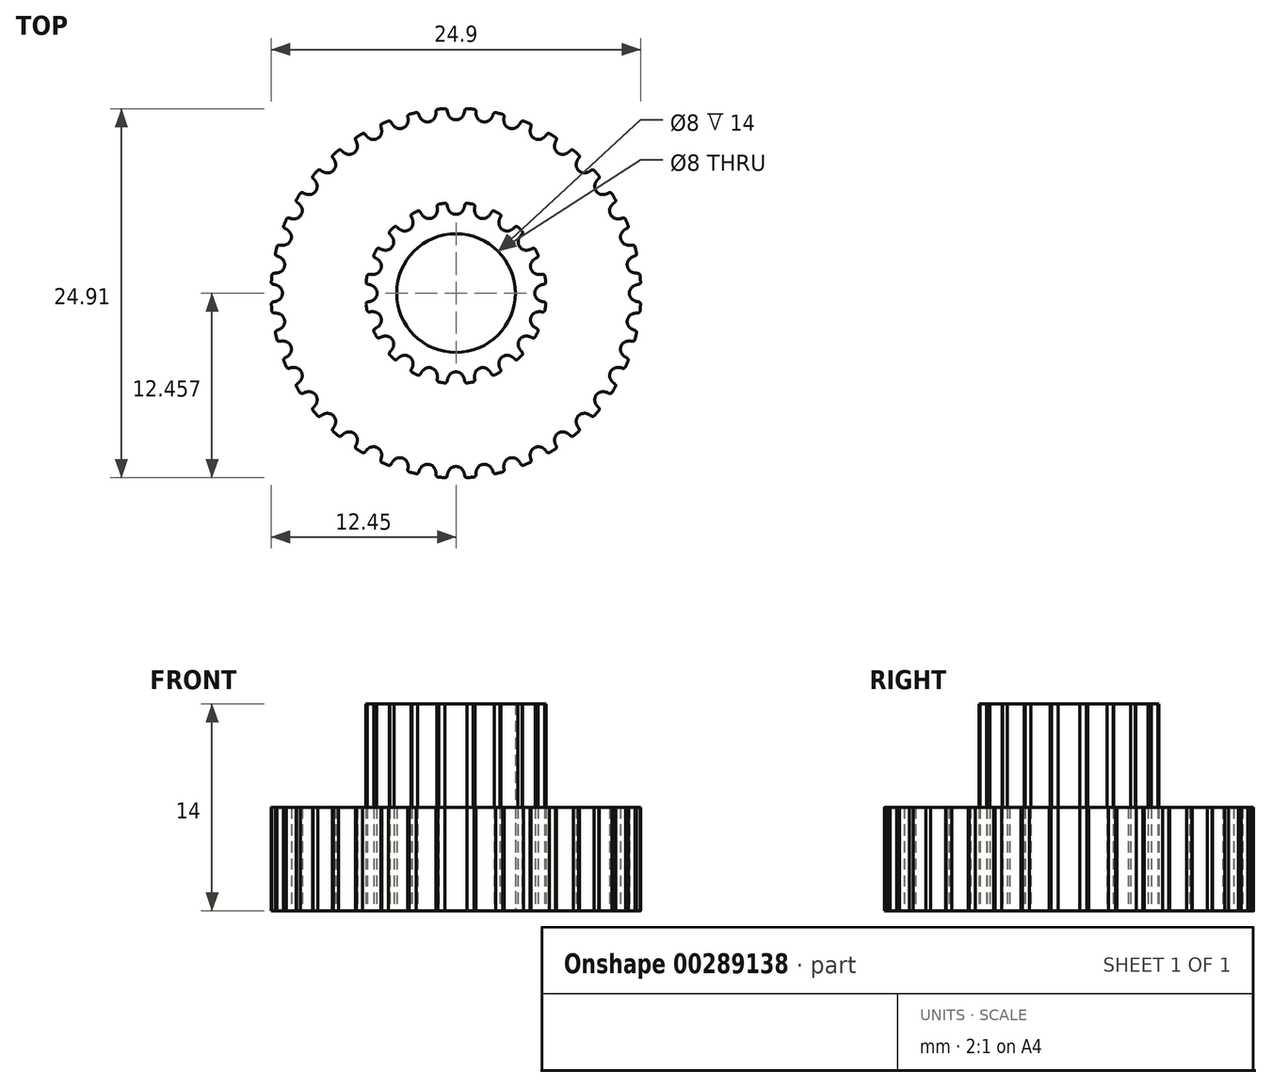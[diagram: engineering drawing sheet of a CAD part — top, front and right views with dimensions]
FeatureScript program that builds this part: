
annotation { "Feature Type Name" : "Feature", "Feature Type Description" : "" }
export const myFeature = defineFeature(function(context is Context, id is Id, definition is map)
    precondition{}
    {
        {
            var Q0;
            Q0=qCreatedBy(makeId("Top.planeOp"),FACE);
            var sketch = newSketch(context, id + "F0", { "sketchPlane" : qUnion([Q0])});
            skLineSegment(sketch, "E0", {"start": v(0, 0) * mm, "end": v(0, -1.46) * mm, "construction": true});
            skArc(sketch, "E1", {"start": v(1.22, 12.21) * mm, "mid": v(0.98, 12.23) * mm, "end": v(0.74, 12.25) * mm});
            skArc(sketch, "E2", {"start": v(-0.5, 11.81) * mm, "mid": v(-0.3, 11.58) * mm, "end": v(0, 11.5) * mm});
            skArc(sketch, "E3", {"start": v(-0.6, 12.12) * mm, "mid": v(-0.56, 11.96) * mm, "end": v(-0.5, 11.81) * mm});
            skArc(sketch, "E4", {"start": v(-0.6, 12.12) * mm, "mid": v(-0.64, 12.21) * mm, "end": v(-0.74, 12.25) * mm});
            skArc(sketch, "E5", {"start": v(0, 11.5) * mm, "mid": v(0.3, 11.58) * mm, "end": v(0.5, 11.81) * mm});
            skArc(sketch, "E6", {"start": v(0.5, 11.81) * mm, "mid": v(0.56, 11.96) * mm, "end": v(0.6, 12.12) * mm});
            skArc(sketch, "E7", {"start": v(0.74, 12.25) * mm, "mid": v(0.64, 12.21) * mm, "end": v(0.6, 12.12) * mm});
            skArc(sketch, "E8", {"start": v(-2.37, 11.59) * mm, "mid": v(-2.13, 11.4) * mm, "end": v(-1.83, 11.36) * mm});
            skArc(sketch, "E9", {"start": v(-2.51, 11.88) * mm, "mid": v(-2.45, 11.73) * mm, "end": v(-2.37, 11.59) * mm});
            skArc(sketch, "E10", {"start": v(-2.51, 11.88) * mm, "mid": v(-2.58, 11.96) * mm, "end": v(-2.68, 11.98) * mm});
            skArc(sketch, "E11", {"start": v(-1.83, 11.36) * mm, "mid": v(-1.55, 11.49) * mm, "end": v(-1.39, 11.74) * mm});
            skArc(sketch, "E12", {"start": v(-1.39, 11.74) * mm, "mid": v(-1.35, 11.9) * mm, "end": v(-1.34, 12.06) * mm});
            skArc(sketch, "E13", {"start": v(-1.22, 12.21) * mm, "mid": v(-1.3, 12.16) * mm, "end": v(-1.34, 12.06) * mm});
            skArc(sketch, "E14", {"start": v(-4.19, 11.07) * mm, "mid": v(-3.92, 10.92) * mm, "end": v(-3.62, 10.93) * mm});
            skArc(sketch, "E15", {"start": v(-4.37, 11.33) * mm, "mid": v(-4.29, 11.2) * mm, "end": v(-4.19, 11.07) * mm});
            skArc(sketch, "E16", {"start": v(-4.37, 11.33) * mm, "mid": v(-4.45, 11.4) * mm, "end": v(-4.55, 11.41) * mm});
            skArc(sketch, "E17", {"start": v(-3.62, 10.93) * mm, "mid": v(-3.36, 11.1) * mm, "end": v(-3.24, 11.38) * mm});
            skArc(sketch, "E18", {"start": v(-3.24, 11.38) * mm, "mid": v(-3.23, 11.54) * mm, "end": v(-3.25, 11.7) * mm});
            skArc(sketch, "E19", {"start": v(-3.14, 11.87) * mm, "mid": v(-3.23, 11.8) * mm, "end": v(-3.25, 11.7) * mm});
            skArc(sketch, "E20", {"start": v(-5.9, 10.28) * mm, "mid": v(-5.61, 10.17) * mm, "end": v(-5.31, 10.22) * mm});
            skArc(sketch, "E21", {"start": v(-6.12, 10.5) * mm, "mid": v(-6.02, 10.38) * mm, "end": v(-5.9, 10.28) * mm});
            skArc(sketch, "E22", {"start": v(-6.12, 10.5) * mm, "mid": v(-6.2, 10.57) * mm, "end": v(-6.31, 10.56) * mm});
            skArc(sketch, "E23", {"start": v(-5.31, 10.22) * mm, "mid": v(-5.09, 10.43) * mm, "end": v(-5.01, 10.73) * mm});
            skArc(sketch, "E24", {"start": v(-5.01, 10.73) * mm, "mid": v(-5.03, 10.89) * mm, "end": v(-5.07, 11.05) * mm});
            skArc(sketch, "E25", {"start": v(-5, 11.23) * mm, "mid": v(-5.07, 11.15) * mm, "end": v(-5.07, 11.05) * mm});
            skArc(sketch, "E26", {"start": v(-7.47, 9.22) * mm, "mid": v(-7.17, 9.16) * mm, "end": v(-6.88, 9.27) * mm});
            skArc(sketch, "E27", {"start": v(-7.72, 9.42) * mm, "mid": v(-7.6, 9.31) * mm, "end": v(-7.47, 9.22) * mm});
            skArc(sketch, "E28", {"start": v(-7.72, 9.42) * mm, "mid": v(-7.82, 9.46) * mm, "end": v(-7.92, 9.44) * mm});
            skArc(sketch, "E29", {"start": v(-6.88, 9.27) * mm, "mid": v(-6.7, 9.5) * mm, "end": v(-6.66, 9.81) * mm});
            skArc(sketch, "E30", {"start": v(-6.66, 9.81) * mm, "mid": v(-6.7, 9.97) * mm, "end": v(-6.76, 10.11) * mm});
            skArc(sketch, "E31", {"start": v(-6.72, 10.3) * mm, "mid": v(-6.78, 10.22) * mm, "end": v(-6.76, 10.11) * mm});
            skArc(sketch, "E32", {"start": v(-8.85, 7.94) * mm, "mid": v(-8.54, 7.92) * mm, "end": v(-8.28, 8.07) * mm});
            skArc(sketch, "E33", {"start": v(-9.13, 8.1) * mm, "mid": v(-9, 8) * mm, "end": v(-8.85, 7.94) * mm});
            skArc(sketch, "E34", {"start": v(-9.13, 8.1) * mm, "mid": v(-9.23, 8.12) * mm, "end": v(-9.33, 8.08) * mm});
            skArc(sketch, "E35", {"start": v(-8.28, 8.07) * mm, "mid": v(-8.13, 8.34) * mm, "end": v(-8.14, 8.65) * mm});
            skArc(sketch, "E36", {"start": v(-8.14, 8.65) * mm, "mid": v(-8.2, 8.8) * mm, "end": v(-8.3, 8.93) * mm});
            skArc(sketch, "E37", {"start": v(-8.28, 9.13) * mm, "mid": v(-8.33, 9.03) * mm, "end": v(-8.3, 8.93) * mm});
            skArc(sketch, "E38", {"start": v(-10.01, 6.46) * mm, "mid": v(-9.7, 6.49) * mm, "end": v(-9.47, 6.68) * mm});
            skArc(sketch, "E39", {"start": v(-10.32, 6.56) * mm, "mid": v(-10.17, 6.5) * mm, "end": v(-10.01, 6.46) * mm});
            skArc(sketch, "E40", {"start": v(-10.32, 6.56) * mm, "mid": v(-10.42, 6.58) * mm, "end": v(-10.5, 6.52) * mm});
            skArc(sketch, "E41", {"start": v(-9.47, 6.68) * mm, "mid": v(-9.36, 6.96) * mm, "end": v(-9.43, 7.26) * mm});
            skArc(sketch, "E42", {"start": v(-9.43, 7.26) * mm, "mid": v(-9.51, 7.4) * mm, "end": v(-9.62, 7.52) * mm});
            skArc(sketch, "E43", {"start": v(-9.64, 7.72) * mm, "mid": v(-9.67, 7.61) * mm, "end": v(-9.62, 7.52) * mm});
            skArc(sketch, "E44", {"start": v(-10.93, 4.8) * mm, "mid": v(-10.64, 4.89) * mm, "end": v(-10.43, 5.11) * mm});
            skArc(sketch, "E45", {"start": v(-11.25, 4.86) * mm, "mid": v(-11.1, 4.82) * mm, "end": v(-10.93, 4.8) * mm});
            skArc(sketch, "E46", {"start": v(-11.25, 4.86) * mm, "mid": v(-11.35, 4.86) * mm, "end": v(-11.43, 4.8) * mm});
            skArc(sketch, "E47", {"start": v(-10.43, 5.11) * mm, "mid": v(-10.37, 5.41) * mm, "end": v(-10.48, 5.7) * mm});
            skArc(sketch, "E48", {"start": v(-10.48, 5.7) * mm, "mid": v(-10.59, 5.82) * mm, "end": v(-10.71, 5.92) * mm});
            skArc(sketch, "E49", {"start": v(-10.76, 6.11) * mm, "mid": v(-10.77, 6) * mm, "end": v(-10.71, 5.92) * mm});
            skArc(sketch, "E50", {"start": v(-11.58, 3.04) * mm, "mid": v(-11.3, 3.16) * mm, "end": v(-11.13, 3.41) * mm});
            skArc(sketch, "E51", {"start": v(-11.9, 3.04) * mm, "mid": v(-11.74, 3.03) * mm, "end": v(-11.58, 3.04) * mm});
            skArc(sketch, "E52", {"start": v(-11.9, 3.04) * mm, "mid": v(-12, 3.02) * mm, "end": v(-12.07, 2.94) * mm});
            skArc(sketch, "E53", {"start": v(-11.13, 3.41) * mm, "mid": v(-11.12, 3.72) * mm, "end": v(-11.27, 3.98) * mm});
            skArc(sketch, "E54", {"start": v(-11.27, 3.98) * mm, "mid": v(-11.4, 4.09) * mm, "end": v(-11.54, 4.17) * mm});
            skArc(sketch, "E55", {"start": v(-11.61, 4.35) * mm, "mid": v(-11.6, 4.24) * mm, "end": v(-11.54, 4.17) * mm});
            skArc(sketch, "E56", {"start": v(-11.94, 1.18) * mm, "mid": v(-11.69, 1.35) * mm, "end": v(-11.56, 1.63) * mm});
            skArc(sketch, "E57", {"start": v(-12.26, 1.14) * mm, "mid": v(-12.1, 1.15) * mm, "end": v(-11.94, 1.18) * mm});
            skArc(sketch, "E58", {"start": v(-12.26, 1.14) * mm, "mid": v(-12.36, 1.1) * mm, "end": v(-12.42, 1.01) * mm});
            skArc(sketch, "E59", {"start": v(-11.56, 1.63) * mm, "mid": v(-11.6, 1.93) * mm, "end": v(-11.79, 2.17) * mm});
            skArc(sketch, "E60", {"start": v(-11.79, 2.17) * mm, "mid": v(-11.93, 2.25) * mm, "end": v(-12.08, 2.3) * mm});
            skArc(sketch, "E61", {"start": v(-12.18, 2.48) * mm, "mid": v(-12.16, 2.37) * mm, "end": v(-12.08, 2.3) * mm});
            skArc(sketch, "E62", {"start": v(-12.01, -0.7) * mm, "mid": v(-11.79, -0.5) * mm, "end": v(-11.7, -0.2) * mm});
            skArc(sketch, "E63", {"start": v(-12.32, -0.8) * mm, "mid": v(-12.16, -0.76) * mm, "end": v(-12.01, -0.7) * mm});
            skArc(sketch, "E64", {"start": v(-12.32, -0.8) * mm, "mid": v(-12.42, -0.84) * mm, "end": v(-12.45, -0.94) * mm});
            skArc(sketch, "E65", {"start": v(-11.7, -0.2) * mm, "mid": v(-11.79, 0.1) * mm, "end": v(-12.01, 0.3) * mm});
            skArc(sketch, "E66", {"start": v(-12.01, 0.3) * mm, "mid": v(-12.16, 0.35) * mm, "end": v(-12.32, 0.39) * mm});
            skArc(sketch, "E67", {"start": v(-12.45, 0.54) * mm, "mid": v(-12.42, 0.44) * mm, "end": v(-12.32, 0.39) * mm});
            skArc(sketch, "E68", {"start": v(-11.79, -2.58) * mm, "mid": v(-11.6, -2.34) * mm, "end": v(-11.56, -2.03) * mm});
            skArc(sketch, "E69", {"start": v(-12.08, -2.71) * mm, "mid": v(-11.93, -2.66) * mm, "end": v(-11.79, -2.58) * mm});
            skArc(sketch, "E70", {"start": v(-12.08, -2.71) * mm, "mid": v(-12.16, -2.78) * mm, "end": v(-12.18, -2.88) * mm});
            skArc(sketch, "E71", {"start": v(-11.56, -2.03) * mm, "mid": v(-11.69, -1.76) * mm, "end": v(-11.94, -1.59) * mm});
            skArc(sketch, "E72", {"start": v(-11.94, -1.59) * mm, "mid": v(-12.1, -1.56) * mm, "end": v(-12.26, -1.55) * mm});
            skArc(sketch, "E73", {"start": v(-12.42, -1.42) * mm, "mid": v(-12.36, -1.51) * mm, "end": v(-12.26, -1.55) * mm});
            skArc(sketch, "E74", {"start": v(-11.27, -4.4) * mm, "mid": v(-11.12, -4.13) * mm, "end": v(-11.13, -3.82) * mm});
            skArc(sketch, "E75", {"start": v(-11.54, -4.57) * mm, "mid": v(-11.4, -4.5) * mm, "end": v(-11.27, -4.4) * mm});
            skArc(sketch, "E76", {"start": v(-11.54, -4.57) * mm, "mid": v(-11.6, -4.65) * mm, "end": v(-11.61, -4.75) * mm});
            skArc(sketch, "E77", {"start": v(-11.13, -3.82) * mm, "mid": v(-11.3, -3.57) * mm, "end": v(-11.58, -3.44) * mm});
            skArc(sketch, "E78", {"start": v(-11.58, -3.44) * mm, "mid": v(-11.74, -3.43) * mm, "end": v(-11.9, -3.45) * mm});
            skArc(sketch, "E79", {"start": v(-12.07, -3.35) * mm, "mid": v(-12, -3.43) * mm, "end": v(-11.9, -3.45) * mm});
            skArc(sketch, "E80", {"start": v(-10.48, -6.1) * mm, "mid": v(-10.37, -5.82) * mm, "end": v(-10.43, -5.52) * mm});
            skArc(sketch, "E81", {"start": v(-10.71, -6.32) * mm, "mid": v(-10.59, -6.22) * mm, "end": v(-10.48, -6.1) * mm});
            skArc(sketch, "E82", {"start": v(-10.71, -6.32) * mm, "mid": v(-10.77, -6.41) * mm, "end": v(-10.76, -6.52) * mm});
            skArc(sketch, "E83", {"start": v(-10.43, -5.52) * mm, "mid": v(-10.64, -5.3) * mm, "end": v(-10.93, -5.21) * mm});
            skArc(sketch, "E84", {"start": v(-10.93, -5.21) * mm, "mid": v(-11.1, -5.23) * mm, "end": v(-11.25, -5.27) * mm});
            skArc(sketch, "E85", {"start": v(-11.43, -5.2) * mm, "mid": v(-11.35, -5.27) * mm, "end": v(-11.25, -5.27) * mm});
            skArc(sketch, "E86", {"start": v(-9.43, -7.67) * mm, "mid": v(-9.36, -7.37) * mm, "end": v(-9.47, -7.08) * mm});
            skArc(sketch, "E87", {"start": v(-9.62, -7.92) * mm, "mid": v(-9.51, -7.8) * mm, "end": v(-9.43, -7.67) * mm});
            skArc(sketch, "E88", {"start": v(-9.62, -7.92) * mm, "mid": v(-9.67, -8.02) * mm, "end": v(-9.64, -8.12) * mm});
            skArc(sketch, "E89", {"start": v(-9.47, -7.08) * mm, "mid": v(-9.7, -6.9) * mm, "end": v(-10.01, -6.86) * mm});
            skArc(sketch, "E90", {"start": v(-10.01, -6.86) * mm, "mid": v(-10.17, -6.9) * mm, "end": v(-10.32, -6.97) * mm});
            skArc(sketch, "E91", {"start": v(-10.5, -6.92) * mm, "mid": v(-10.42, -6.98) * mm, "end": v(-10.32, -6.97) * mm});
            skArc(sketch, "E92", {"start": v(-8.14, -9.05) * mm, "mid": v(-8.13, -8.75) * mm, "end": v(-8.28, -8.48) * mm});
            skArc(sketch, "E93", {"start": v(-8.3, -9.33) * mm, "mid": v(-8.2, -9.2) * mm, "end": v(-8.14, -9.05) * mm});
            skArc(sketch, "E94", {"start": v(-8.3, -9.33) * mm, "mid": v(-8.33, -9.44) * mm, "end": v(-8.28, -9.53) * mm});
            skArc(sketch, "E95", {"start": v(-8.28, -8.48) * mm, "mid": v(-8.54, -8.33) * mm, "end": v(-8.85, -8.35) * mm});
            skArc(sketch, "E96", {"start": v(-8.85, -8.35) * mm, "mid": v(-9, -8.41) * mm, "end": v(-9.13, -8.5) * mm});
            skArc(sketch, "E97", {"start": v(-9.33, -8.49) * mm, "mid": v(-9.23, -8.53) * mm, "end": v(-9.13, -8.5) * mm});
            skArc(sketch, "E98", {"start": v(-6.66, -10.22) * mm, "mid": v(-6.7, -9.91) * mm, "end": v(-6.88, -9.67) * mm});
            skArc(sketch, "E99", {"start": v(-6.76, -10.52) * mm, "mid": v(-6.7, -10.37) * mm, "end": v(-6.66, -10.22) * mm});
            skArc(sketch, "E100", {"start": v(-6.76, -10.52) * mm, "mid": v(-6.78, -10.62) * mm, "end": v(-6.72, -10.71) * mm});
            skArc(sketch, "E101", {"start": v(-6.88, -9.67) * mm, "mid": v(-7.17, -9.57) * mm, "end": v(-7.47, -9.63) * mm});
            skArc(sketch, "E102", {"start": v(-7.47, -9.63) * mm, "mid": v(-7.6, -9.72) * mm, "end": v(-7.72, -9.82) * mm});
            skArc(sketch, "E103", {"start": v(-7.92, -9.84) * mm, "mid": v(-7.82, -9.87) * mm, "end": v(-7.72, -9.82) * mm});
            skArc(sketch, "E104", {"start": v(-5.01, -11.13) * mm, "mid": v(-5.09, -10.84) * mm, "end": v(-5.31, -10.63) * mm});
            skArc(sketch, "E105", {"start": v(-5.07, -11.45) * mm, "mid": v(-5.03, -11.3) * mm, "end": v(-5.01, -11.13) * mm});
            skArc(sketch, "E106", {"start": v(-5.07, -11.45) * mm, "mid": v(-5.07, -11.56) * mm, "end": v(-5, -11.63) * mm});
            skArc(sketch, "E107", {"start": v(-5.31, -10.63) * mm, "mid": v(-5.61, -10.57) * mm, "end": v(-5.9, -10.68) * mm});
            skArc(sketch, "E108", {"start": v(-5.9, -10.68) * mm, "mid": v(-6.02, -10.79) * mm, "end": v(-6.12, -10.91) * mm});
            skArc(sketch, "E109", {"start": v(-6.31, -10.96) * mm, "mid": v(-6.2, -10.97) * mm, "end": v(-6.12, -10.91) * mm});
            skArc(sketch, "E110", {"start": v(-3.24, -11.78) * mm, "mid": v(-3.36, -11.5) * mm, "end": v(-3.62, -11.33) * mm});
            skArc(sketch, "E111", {"start": v(-3.25, -12.1) * mm, "mid": v(-3.23, -11.94) * mm, "end": v(-3.24, -11.78) * mm});
            skArc(sketch, "E112", {"start": v(-3.25, -12.1) * mm, "mid": v(-3.23, -12.2) * mm, "end": v(-3.14, -12.28) * mm});
            skArc(sketch, "E113", {"start": v(-3.62, -11.33) * mm, "mid": v(-3.92, -11.32) * mm, "end": v(-4.19, -11.48) * mm});
            skArc(sketch, "E114", {"start": v(-4.19, -11.48) * mm, "mid": v(-4.29, -11.6) * mm, "end": v(-4.37, -11.74) * mm});
            skArc(sketch, "E115", {"start": v(-4.55, -11.82) * mm, "mid": v(-4.45, -11.81) * mm, "end": v(-4.37, -11.74) * mm});
            skArc(sketch, "E116", {"start": v(-1.39, -12.15) * mm, "mid": v(-1.55, -11.9) * mm, "end": v(-1.83, -11.76) * mm});
            skArc(sketch, "E117", {"start": v(-1.34, -12.47) * mm, "mid": v(-1.35, -12.3) * mm, "end": v(-1.39, -12.15) * mm});
            skArc(sketch, "E118", {"start": v(-1.34, -12.47) * mm, "mid": v(-1.3, -12.57) * mm, "end": v(-1.22, -12.62) * mm});
            skArc(sketch, "E119", {"start": v(-1.83, -11.76) * mm, "mid": v(-2.13, -11.8) * mm, "end": v(-2.37, -12) * mm});
            skArc(sketch, "E120", {"start": v(-2.37, -12) * mm, "mid": v(-2.45, -12.13) * mm, "end": v(-2.51, -12.28) * mm});
            skArc(sketch, "E121", {"start": v(-2.68, -12.39) * mm, "mid": v(-2.58, -12.37) * mm, "end": v(-2.51, -12.28) * mm});
            skArc(sketch, "E122", {"start": v(0.5, -12.22) * mm, "mid": v(0.3, -12) * mm, "end": v(0, -11.9) * mm});
            skArc(sketch, "E123", {"start": v(0.6, -12.53) * mm, "mid": v(0.56, -12.37) * mm, "end": v(0.5, -12.22) * mm});
            skArc(sketch, "E124", {"start": v(0.6, -12.53) * mm, "mid": v(0.64, -12.62) * mm, "end": v(0.74, -12.66) * mm});
            skArc(sketch, "E125", {"start": v(0, -11.9) * mm, "mid": v(-0.3, -12) * mm, "end": v(-0.5, -12.22) * mm});
            skArc(sketch, "E126", {"start": v(-0.5, -12.22) * mm, "mid": v(-0.56, -12.37) * mm, "end": v(-0.6, -12.53) * mm});
            skArc(sketch, "E127", {"start": v(-0.74, -12.66) * mm, "mid": v(-0.64, -12.62) * mm, "end": v(-0.6, -12.53) * mm});
            skArc(sketch, "E128", {"start": v(2.37, -12) * mm, "mid": v(2.13, -11.8) * mm, "end": v(1.83, -11.76) * mm});
            skArc(sketch, "E129", {"start": v(2.51, -12.28) * mm, "mid": v(2.45, -12.13) * mm, "end": v(2.37, -12) * mm});
            skArc(sketch, "E130", {"start": v(2.51, -12.28) * mm, "mid": v(2.58, -12.37) * mm, "end": v(2.68, -12.39) * mm});
            skArc(sketch, "E131", {"start": v(1.83, -11.76) * mm, "mid": v(1.55, -11.9) * mm, "end": v(1.39, -12.15) * mm});
            skArc(sketch, "E132", {"start": v(1.39, -12.15) * mm, "mid": v(1.35, -12.3) * mm, "end": v(1.34, -12.47) * mm});
            skArc(sketch, "E133", {"start": v(1.22, -12.62) * mm, "mid": v(1.3, -12.57) * mm, "end": v(1.34, -12.47) * mm});
            skArc(sketch, "E134", {"start": v(4.19, -11.48) * mm, "mid": v(3.92, -11.32) * mm, "end": v(3.62, -11.33) * mm});
            skArc(sketch, "E135", {"start": v(4.37, -11.74) * mm, "mid": v(4.29, -11.6) * mm, "end": v(4.19, -11.48) * mm});
            skArc(sketch, "E136", {"start": v(4.37, -11.74) * mm, "mid": v(4.45, -11.81) * mm, "end": v(4.55, -11.82) * mm});
            skArc(sketch, "E137", {"start": v(3.62, -11.33) * mm, "mid": v(3.36, -11.5) * mm, "end": v(3.24, -11.78) * mm});
            skArc(sketch, "E138", {"start": v(3.24, -11.78) * mm, "mid": v(3.23, -11.94) * mm, "end": v(3.25, -12.1) * mm});
            skArc(sketch, "E139", {"start": v(3.14, -12.28) * mm, "mid": v(3.23, -12.2) * mm, "end": v(3.25, -12.1) * mm});
            skArc(sketch, "E140", {"start": v(5.9, -10.68) * mm, "mid": v(5.61, -10.57) * mm, "end": v(5.31, -10.63) * mm});
            skArc(sketch, "E141", {"start": v(6.12, -10.91) * mm, "mid": v(6.02, -10.79) * mm, "end": v(5.9, -10.68) * mm});
            skArc(sketch, "E142", {"start": v(6.12, -10.91) * mm, "mid": v(6.2, -10.97) * mm, "end": v(6.31, -10.96) * mm});
            skArc(sketch, "E143", {"start": v(5.31, -10.63) * mm, "mid": v(5.09, -10.84) * mm, "end": v(5.01, -11.13) * mm});
            skArc(sketch, "E144", {"start": v(5.01, -11.13) * mm, "mid": v(5.03, -11.3) * mm, "end": v(5.07, -11.45) * mm});
            skArc(sketch, "E145", {"start": v(5, -11.63) * mm, "mid": v(5.07, -11.56) * mm, "end": v(5.07, -11.45) * mm});
            skArc(sketch, "E146", {"start": v(7.47, -9.63) * mm, "mid": v(7.17, -9.57) * mm, "end": v(6.88, -9.67) * mm});
            skArc(sketch, "E147", {"start": v(7.72, -9.82) * mm, "mid": v(7.6, -9.72) * mm, "end": v(7.47, -9.63) * mm});
            skArc(sketch, "E148", {"start": v(7.72, -9.82) * mm, "mid": v(7.82, -9.87) * mm, "end": v(7.92, -9.84) * mm});
            skArc(sketch, "E149", {"start": v(6.88, -9.67) * mm, "mid": v(6.7, -9.91) * mm, "end": v(6.66, -10.22) * mm});
            skArc(sketch, "E150", {"start": v(6.66, -10.22) * mm, "mid": v(6.7, -10.37) * mm, "end": v(6.76, -10.52) * mm});
            skArc(sketch, "E151", {"start": v(6.72, -10.71) * mm, "mid": v(6.78, -10.62) * mm, "end": v(6.76, -10.52) * mm});
            skArc(sketch, "E152", {"start": v(8.85, -8.35) * mm, "mid": v(8.54, -8.33) * mm, "end": v(8.28, -8.48) * mm});
            skArc(sketch, "E153", {"start": v(9.13, -8.5) * mm, "mid": v(9, -8.41) * mm, "end": v(8.85, -8.35) * mm});
            skArc(sketch, "E154", {"start": v(9.13, -8.5) * mm, "mid": v(9.23, -8.53) * mm, "end": v(9.33, -8.49) * mm});
            skArc(sketch, "E155", {"start": v(8.28, -8.48) * mm, "mid": v(8.13, -8.75) * mm, "end": v(8.14, -9.05) * mm});
            skArc(sketch, "E156", {"start": v(8.14, -9.05) * mm, "mid": v(8.2, -9.2) * mm, "end": v(8.3, -9.33) * mm});
            skArc(sketch, "E157", {"start": v(8.28, -9.53) * mm, "mid": v(8.33, -9.44) * mm, "end": v(8.3, -9.33) * mm});
            skArc(sketch, "E158", {"start": v(10.01, -6.86) * mm, "mid": v(9.7, -6.9) * mm, "end": v(9.47, -7.08) * mm});
            skArc(sketch, "E159", {"start": v(10.32, -6.97) * mm, "mid": v(10.17, -6.9) * mm, "end": v(10.01, -6.86) * mm});
            skArc(sketch, "E160", {"start": v(10.32, -6.97) * mm, "mid": v(10.42, -6.98) * mm, "end": v(10.5, -6.92) * mm});
            skArc(sketch, "E161", {"start": v(9.47, -7.08) * mm, "mid": v(9.36, -7.37) * mm, "end": v(9.43, -7.67) * mm});
            skArc(sketch, "E162", {"start": v(9.43, -7.67) * mm, "mid": v(9.51, -7.8) * mm, "end": v(9.62, -7.92) * mm});
            skArc(sketch, "E163", {"start": v(9.64, -8.12) * mm, "mid": v(9.67, -8.02) * mm, "end": v(9.62, -7.92) * mm});
            skArc(sketch, "E164", {"start": v(10.93, -5.21) * mm, "mid": v(10.64, -5.3) * mm, "end": v(10.43, -5.52) * mm});
            skArc(sketch, "E165", {"start": v(11.25, -5.27) * mm, "mid": v(11.1, -5.23) * mm, "end": v(10.93, -5.21) * mm});
            skArc(sketch, "E166", {"start": v(11.25, -5.27) * mm, "mid": v(11.35, -5.27) * mm, "end": v(11.43, -5.2) * mm});
            skArc(sketch, "E167", {"start": v(10.43, -5.52) * mm, "mid": v(10.37, -5.82) * mm, "end": v(10.48, -6.1) * mm});
            skArc(sketch, "E168", {"start": v(10.48, -6.1) * mm, "mid": v(10.59, -6.22) * mm, "end": v(10.71, -6.32) * mm});
            skArc(sketch, "E169", {"start": v(10.76, -6.52) * mm, "mid": v(10.77, -6.41) * mm, "end": v(10.71, -6.32) * mm});
            skArc(sketch, "E170", {"start": v(11.58, -3.44) * mm, "mid": v(11.3, -3.57) * mm, "end": v(11.13, -3.82) * mm});
            skArc(sketch, "E171", {"start": v(11.9, -3.45) * mm, "mid": v(11.74, -3.43) * mm, "end": v(11.58, -3.44) * mm});
            skArc(sketch, "E172", {"start": v(11.9, -3.45) * mm, "mid": v(12, -3.43) * mm, "end": v(12.07, -3.35) * mm});
            skArc(sketch, "E173", {"start": v(11.13, -3.82) * mm, "mid": v(11.12, -4.13) * mm, "end": v(11.27, -4.4) * mm});
            skArc(sketch, "E174", {"start": v(11.27, -4.4) * mm, "mid": v(11.4, -4.5) * mm, "end": v(11.54, -4.57) * mm});
            skArc(sketch, "E175", {"start": v(11.61, -4.75) * mm, "mid": v(11.6, -4.65) * mm, "end": v(11.54, -4.57) * mm});
            skArc(sketch, "E176", {"start": v(11.94, -1.59) * mm, "mid": v(11.69, -1.76) * mm, "end": v(11.56, -2.03) * mm});
            skArc(sketch, "E177", {"start": v(12.26, -1.55) * mm, "mid": v(12.1, -1.56) * mm, "end": v(11.94, -1.59) * mm});
            skArc(sketch, "E178", {"start": v(12.26, -1.55) * mm, "mid": v(12.36, -1.51) * mm, "end": v(12.42, -1.42) * mm});
            skArc(sketch, "E179", {"start": v(11.56, -2.03) * mm, "mid": v(11.6, -2.34) * mm, "end": v(11.79, -2.58) * mm});
            skArc(sketch, "E180", {"start": v(11.79, -2.58) * mm, "mid": v(11.93, -2.66) * mm, "end": v(12.08, -2.71) * mm});
            skArc(sketch, "E181", {"start": v(12.18, -2.88) * mm, "mid": v(12.16, -2.78) * mm, "end": v(12.08, -2.71) * mm});
            skArc(sketch, "E182", {"start": v(12.01, 0.3) * mm, "mid": v(11.79, 0.1) * mm, "end": v(11.7, -0.2) * mm});
            skArc(sketch, "E183", {"start": v(12.32, 0.39) * mm, "mid": v(12.16, 0.35) * mm, "end": v(12.01, 0.3) * mm});
            skArc(sketch, "E184", {"start": v(12.32, 0.39) * mm, "mid": v(12.42, 0.44) * mm, "end": v(12.45, 0.54) * mm});
            skArc(sketch, "E185", {"start": v(11.7, -0.2) * mm, "mid": v(11.79, -0.5) * mm, "end": v(12.01, -0.7) * mm});
            skArc(sketch, "E186", {"start": v(12.01, -0.7) * mm, "mid": v(12.16, -0.76) * mm, "end": v(12.32, -0.8) * mm});
            skArc(sketch, "E187", {"start": v(12.45, -0.94) * mm, "mid": v(12.42, -0.84) * mm, "end": v(12.32, -0.8) * mm});
            skArc(sketch, "E188", {"start": v(11.79, 2.17) * mm, "mid": v(11.6, 1.93) * mm, "end": v(11.56, 1.63) * mm});
            skArc(sketch, "E189", {"start": v(12.08, 2.3) * mm, "mid": v(11.93, 2.25) * mm, "end": v(11.79, 2.17) * mm});
            skArc(sketch, "E190", {"start": v(12.08, 2.3) * mm, "mid": v(12.16, 2.37) * mm, "end": v(12.18, 2.48) * mm});
            skArc(sketch, "E191", {"start": v(11.56, 1.63) * mm, "mid": v(11.69, 1.35) * mm, "end": v(11.94, 1.18) * mm});
            skArc(sketch, "E192", {"start": v(11.94, 1.18) * mm, "mid": v(12.1, 1.15) * mm, "end": v(12.26, 1.14) * mm});
            skArc(sketch, "E193", {"start": v(12.42, 1.01) * mm, "mid": v(12.36, 1.1) * mm, "end": v(12.26, 1.14) * mm});
            skArc(sketch, "E194", {"start": v(11.27, 3.98) * mm, "mid": v(11.12, 3.72) * mm, "end": v(11.13, 3.41) * mm});
            skArc(sketch, "E195", {"start": v(11.54, 4.17) * mm, "mid": v(11.4, 4.09) * mm, "end": v(11.27, 3.98) * mm});
            skArc(sketch, "E196", {"start": v(11.54, 4.17) * mm, "mid": v(11.6, 4.24) * mm, "end": v(11.61, 4.35) * mm});
            skArc(sketch, "E197", {"start": v(11.13, 3.41) * mm, "mid": v(11.3, 3.16) * mm, "end": v(11.58, 3.04) * mm});
            skArc(sketch, "E198", {"start": v(11.58, 3.04) * mm, "mid": v(11.74, 3.03) * mm, "end": v(11.9, 3.04) * mm});
            skArc(sketch, "E199", {"start": v(12.07, 2.94) * mm, "mid": v(12, 3.02) * mm, "end": v(11.9, 3.04) * mm});
            skArc(sketch, "E200", {"start": v(10.48, 5.7) * mm, "mid": v(10.37, 5.41) * mm, "end": v(10.43, 5.11) * mm});
            skArc(sketch, "E201", {"start": v(10.71, 5.92) * mm, "mid": v(10.59, 5.82) * mm, "end": v(10.48, 5.7) * mm});
            skArc(sketch, "E202", {"start": v(10.71, 5.92) * mm, "mid": v(10.77, 6) * mm, "end": v(10.76, 6.11) * mm});
            skArc(sketch, "E203", {"start": v(10.43, 5.11) * mm, "mid": v(10.64, 4.89) * mm, "end": v(10.93, 4.8) * mm});
            skArc(sketch, "E204", {"start": v(10.93, 4.8) * mm, "mid": v(11.1, 4.82) * mm, "end": v(11.25, 4.86) * mm});
            skArc(sketch, "E205", {"start": v(11.43, 4.8) * mm, "mid": v(11.35, 4.86) * mm, "end": v(11.25, 4.86) * mm});
            skArc(sketch, "E206", {"start": v(9.43, 7.26) * mm, "mid": v(9.36, 6.96) * mm, "end": v(9.47, 6.68) * mm});
            skArc(sketch, "E207", {"start": v(9.62, 7.52) * mm, "mid": v(9.51, 7.4) * mm, "end": v(9.43, 7.26) * mm});
            skArc(sketch, "E208", {"start": v(9.62, 7.52) * mm, "mid": v(9.67, 7.61) * mm, "end": v(9.64, 7.72) * mm});
            skArc(sketch, "E209", {"start": v(9.47, 6.68) * mm, "mid": v(9.7, 6.49) * mm, "end": v(10.01, 6.46) * mm});
            skArc(sketch, "E210", {"start": v(10.01, 6.46) * mm, "mid": v(10.17, 6.5) * mm, "end": v(10.32, 6.56) * mm});
            skArc(sketch, "E211", {"start": v(10.5, 6.52) * mm, "mid": v(10.42, 6.58) * mm, "end": v(10.32, 6.56) * mm});
            skArc(sketch, "E212", {"start": v(8.14, 8.65) * mm, "mid": v(8.13, 8.34) * mm, "end": v(8.28, 8.07) * mm});
            skArc(sketch, "E213", {"start": v(8.3, 8.93) * mm, "mid": v(8.2, 8.8) * mm, "end": v(8.14, 8.65) * mm});
            skArc(sketch, "E214", {"start": v(8.3, 8.93) * mm, "mid": v(8.33, 9.03) * mm, "end": v(8.28, 9.13) * mm});
            skArc(sketch, "E215", {"start": v(8.28, 8.07) * mm, "mid": v(8.54, 7.92) * mm, "end": v(8.85, 7.94) * mm});
            skArc(sketch, "E216", {"start": v(8.85, 7.94) * mm, "mid": v(9, 8) * mm, "end": v(9.13, 8.1) * mm});
            skArc(sketch, "E217", {"start": v(9.33, 8.08) * mm, "mid": v(9.23, 8.12) * mm, "end": v(9.13, 8.1) * mm});
            skArc(sketch, "E218", {"start": v(6.66, 9.81) * mm, "mid": v(6.7, 9.5) * mm, "end": v(6.88, 9.27) * mm});
            skArc(sketch, "E219", {"start": v(6.76, 10.11) * mm, "mid": v(6.7, 9.97) * mm, "end": v(6.66, 9.81) * mm});
            skArc(sketch, "E220", {"start": v(6.76, 10.11) * mm, "mid": v(6.78, 10.22) * mm, "end": v(6.72, 10.3) * mm});
            skArc(sketch, "E221", {"start": v(6.88, 9.27) * mm, "mid": v(7.17, 9.16) * mm, "end": v(7.47, 9.22) * mm});
            skArc(sketch, "E222", {"start": v(7.47, 9.22) * mm, "mid": v(7.6, 9.31) * mm, "end": v(7.72, 9.42) * mm});
            skArc(sketch, "E223", {"start": v(7.92, 9.44) * mm, "mid": v(7.82, 9.46) * mm, "end": v(7.72, 9.42) * mm});
            skArc(sketch, "E224", {"start": v(5.01, 10.73) * mm, "mid": v(5.09, 10.43) * mm, "end": v(5.31, 10.22) * mm});
            skArc(sketch, "E225", {"start": v(5.07, 11.05) * mm, "mid": v(5.03, 10.89) * mm, "end": v(5.01, 10.73) * mm});
            skArc(sketch, "E226", {"start": v(5.07, 11.05) * mm, "mid": v(5.07, 11.15) * mm, "end": v(5, 11.23) * mm});
            skArc(sketch, "E227", {"start": v(5.31, 10.22) * mm, "mid": v(5.61, 10.17) * mm, "end": v(5.9, 10.28) * mm});
            skArc(sketch, "E228", {"start": v(5.9, 10.28) * mm, "mid": v(6.02, 10.38) * mm, "end": v(6.12, 10.5) * mm});
            skArc(sketch, "E229", {"start": v(6.31, 10.56) * mm, "mid": v(6.2, 10.57) * mm, "end": v(6.12, 10.5) * mm});
            skArc(sketch, "E230", {"start": v(3.24, 11.38) * mm, "mid": v(3.36, 11.1) * mm, "end": v(3.62, 10.93) * mm});
            skArc(sketch, "E231", {"start": v(3.25, 11.7) * mm, "mid": v(3.23, 11.54) * mm, "end": v(3.24, 11.38) * mm});
            skArc(sketch, "E232", {"start": v(3.25, 11.7) * mm, "mid": v(3.23, 11.8) * mm, "end": v(3.14, 11.87) * mm});
            skArc(sketch, "E233", {"start": v(3.62, 10.93) * mm, "mid": v(3.92, 10.92) * mm, "end": v(4.19, 11.07) * mm});
            skArc(sketch, "E234", {"start": v(4.19, 11.07) * mm, "mid": v(4.29, 11.2) * mm, "end": v(4.37, 11.33) * mm});
            skArc(sketch, "E235", {"start": v(4.55, 11.41) * mm, "mid": v(4.45, 11.4) * mm, "end": v(4.37, 11.33) * mm});
            skArc(sketch, "E236", {"start": v(1.39, 11.74) * mm, "mid": v(1.55, 11.49) * mm, "end": v(1.83, 11.36) * mm});
            skArc(sketch, "E237", {"start": v(1.34, 12.06) * mm, "mid": v(1.35, 11.9) * mm, "end": v(1.39, 11.74) * mm});
            skArc(sketch, "E238", {"start": v(1.34, 12.06) * mm, "mid": v(1.3, 12.16) * mm, "end": v(1.22, 12.21) * mm});
            skArc(sketch, "E239", {"start": v(1.83, 11.36) * mm, "mid": v(2.13, 11.4) * mm, "end": v(2.37, 11.59) * mm});
            skArc(sketch, "E240", {"start": v(2.37, 11.59) * mm, "mid": v(2.45, 11.73) * mm, "end": v(2.51, 11.88) * mm});
            skArc(sketch, "E241", {"start": v(2.68, 11.98) * mm, "mid": v(2.58, 11.96) * mm, "end": v(2.51, 11.88) * mm});
            skArc(sketch, "E242", {"start": v(-10.76, -6.52) * mm, "mid": v(-10.64, -6.72) * mm, "end": v(-10.5, -6.92) * mm});
            skArc(sketch, "E243", {"start": v(-9.64, -8.12) * mm, "mid": v(-9.49, -8.3) * mm, "end": v(-9.33, -8.49) * mm});
            skArc(sketch, "E244", {"start": v(-8.28, -9.53) * mm, "mid": v(-8.1, -9.69) * mm, "end": v(-7.92, -9.84) * mm});
            skArc(sketch, "E245", {"start": v(-6.72, -10.71) * mm, "mid": v(-6.52, -10.84) * mm, "end": v(-6.31, -10.96) * mm});
            skArc(sketch, "E246", {"start": v(-5, -11.63) * mm, "mid": v(-4.77, -11.73) * mm, "end": v(-4.55, -11.82) * mm});
            skArc(sketch, "E247", {"start": v(-3.14, -12.28) * mm, "mid": v(-2.91, -12.33) * mm, "end": v(-2.68, -12.39) * mm});
            skArc(sketch, "E248", {"start": v(-1.22, -12.62) * mm, "mid": v(-0.98, -12.64) * mm, "end": v(-0.74, -12.66) * mm});
            skArc(sketch, "E249", {"start": v(0.74, -12.66) * mm, "mid": v(0.98, -12.64) * mm, "end": v(1.22, -12.62) * mm});
            skArc(sketch, "E250", {"start": v(2.68, -12.39) * mm, "mid": v(2.91, -12.33) * mm, "end": v(3.14, -12.28) * mm});
            skArc(sketch, "E251", {"start": v(4.55, -11.82) * mm, "mid": v(4.77, -11.73) * mm, "end": v(5, -11.63) * mm});
            skArc(sketch, "E252", {"start": v(6.31, -10.96) * mm, "mid": v(6.52, -10.84) * mm, "end": v(6.72, -10.71) * mm});
            skArc(sketch, "E253", {"start": v(7.92, -9.84) * mm, "mid": v(8.1, -9.69) * mm, "end": v(8.28, -9.53) * mm});
            skArc(sketch, "E254", {"start": v(9.33, -8.49) * mm, "mid": v(9.49, -8.3) * mm, "end": v(9.64, -8.12) * mm});
            skArc(sketch, "E255", {"start": v(10.5, -6.92) * mm, "mid": v(10.64, -6.72) * mm, "end": v(10.76, -6.52) * mm});
            skArc(sketch, "E256", {"start": v(11.43, -5.2) * mm, "mid": v(11.53, -4.98) * mm, "end": v(11.61, -4.75) * mm});
            skArc(sketch, "E257", {"start": v(12.07, -3.35) * mm, "mid": v(12.13, -3.12) * mm, "end": v(12.18, -2.88) * mm});
            skArc(sketch, "E258", {"start": v(12.42, -1.42) * mm, "mid": v(12.44, -1.18) * mm, "end": v(12.45, -0.94) * mm});
            skArc(sketch, "E259", {"start": v(12.45, 0.54) * mm, "mid": v(12.44, 0.78) * mm, "end": v(12.42, 1.01) * mm});
            skArc(sketch, "E260", {"start": v(12.18, 2.48) * mm, "mid": v(12.13, 2.7) * mm, "end": v(12.07, 2.94) * mm});
            skArc(sketch, "E261", {"start": v(11.61, 4.35) * mm, "mid": v(11.53, 4.57) * mm, "end": v(11.43, 4.8) * mm});
            skArc(sketch, "E262", {"start": v(10.76, 6.11) * mm, "mid": v(10.64, 6.32) * mm, "end": v(10.5, 6.52) * mm});
            skArc(sketch, "E263", {"start": v(9.64, 7.72) * mm, "mid": v(9.49, 7.9) * mm, "end": v(9.33, 8.08) * mm});
            skArc(sketch, "E264", {"start": v(8.28, 9.13) * mm, "mid": v(8.1, 9.28) * mm, "end": v(7.92, 9.44) * mm});
            skArc(sketch, "E265", {"start": v(6.72, 10.3) * mm, "mid": v(6.52, 10.43) * mm, "end": v(6.31, 10.56) * mm});
            skArc(sketch, "E266", {"start": v(5, 11.23) * mm, "mid": v(4.77, 11.32) * mm, "end": v(4.55, 11.41) * mm});
            skArc(sketch, "E267", {"start": v(3.14, 11.87) * mm, "mid": v(2.91, 11.93) * mm, "end": v(2.68, 11.98) * mm});
            skArc(sketch, "E268", {"start": v(-0.74, 12.25) * mm, "mid": v(-0.98, 12.23) * mm, "end": v(-1.22, 12.21) * mm});
            skArc(sketch, "E269", {"start": v(-2.68, 11.98) * mm, "mid": v(-2.91, 11.93) * mm, "end": v(-3.14, 11.87) * mm});
            skArc(sketch, "E270", {"start": v(-4.55, 11.41) * mm, "mid": v(-4.77, 11.32) * mm, "end": v(-5, 11.23) * mm});
            skArc(sketch, "E271", {"start": v(-6.31, 10.56) * mm, "mid": v(-6.52, 10.43) * mm, "end": v(-6.72, 10.3) * mm});
            skArc(sketch, "E272", {"start": v(-7.92, 9.44) * mm, "mid": v(-8.1, 9.28) * mm, "end": v(-8.28, 9.13) * mm});
            skArc(sketch, "E273", {"start": v(-9.33, 8.08) * mm, "mid": v(-9.49, 7.9) * mm, "end": v(-9.64, 7.72) * mm});
            skArc(sketch, "E274", {"start": v(-10.5, 6.52) * mm, "mid": v(-10.64, 6.32) * mm, "end": v(-10.76, 6.11) * mm});
            skArc(sketch, "E275", {"start": v(-11.43, 4.8) * mm, "mid": v(-11.53, 4.57) * mm, "end": v(-11.61, 4.35) * mm});
            skArc(sketch, "E276", {"start": v(-12.07, 2.94) * mm, "mid": v(-12.13, 2.7) * mm, "end": v(-12.18, 2.48) * mm});
            skArc(sketch, "E277", {"start": v(-12.42, 1.01) * mm, "mid": v(-12.44, 0.78) * mm, "end": v(-12.45, 0.54) * mm});
            skArc(sketch, "E278", {"start": v(-12.45, -0.94) * mm, "mid": v(-12.44, -1.18) * mm, "end": v(-12.42, -1.42) * mm});
            skArc(sketch, "E279", {"start": v(-12.18, -2.88) * mm, "mid": v(-12.13, -3.12) * mm, "end": v(-12.07, -3.35) * mm});
            skArc(sketch, "E280", {"start": v(-11.61, -4.75) * mm, "mid": v(-11.53, -4.98) * mm, "end": v(-11.43, -5.2) * mm});
            skArc(sketch, "E281", {"start": v(-0.5, 5.42) * mm, "mid": v(-0.3, 5.2) * mm, "end": v(0, 5.11) * mm});
            skArc(sketch, "E282", {"start": v(-0.6, 5.73) * mm, "mid": v(-0.56, 5.57) * mm, "end": v(-0.5, 5.42) * mm});
            skArc(sketch, "E283", {"start": v(-0.6, 5.73) * mm, "mid": v(-0.64, 5.82) * mm, "end": v(-0.74, 5.86) * mm});
            skArc(sketch, "E284", {"start": v(0, 5.11) * mm, "mid": v(0.3, 5.2) * mm, "end": v(0.5, 5.42) * mm});
            skArc(sketch, "E285", {"start": v(0.5, 5.42) * mm, "mid": v(0.56, 5.57) * mm, "end": v(0.6, 5.73) * mm});
            skArc(sketch, "E286", {"start": v(0.74, 5.86) * mm, "mid": v(0.64, 5.82) * mm, "end": v(0.6, 5.73) * mm});
            skArc(sketch, "E287", {"start": v(-2.21, 5) * mm, "mid": v(-1.95, 4.84) * mm, "end": v(-1.64, 4.85) * mm});
            skArc(sketch, "E288", {"start": v(-2.4, 5.26) * mm, "mid": v(-2.32, 5.12) * mm, "end": v(-2.21, 5) * mm});
            skArc(sketch, "E289", {"start": v(-2.4, 5.26) * mm, "mid": v(-2.47, 5.33) * mm, "end": v(-2.58, 5.34) * mm});
            skArc(sketch, "E290", {"start": v(-1.64, 4.85) * mm, "mid": v(-1.39, 5.02) * mm, "end": v(-1.26, 5.3) * mm});
            skArc(sketch, "E291", {"start": v(-1.26, 5.3) * mm, "mid": v(-1.25, 5.46) * mm, "end": v(-1.27, 5.62) * mm});
            skArc(sketch, "E292", {"start": v(-1.17, 5.8) * mm, "mid": v(-1.25, 5.73) * mm, "end": v(-1.27, 5.62) * mm});
            skArc(sketch, "E293", {"start": v(-3.71, 4.06) * mm, "mid": v(-3.41, 4) * mm, "end": v(-3.12, 4.1) * mm});
            skArc(sketch, "E294", {"start": v(-3.97, 4.25) * mm, "mid": v(-3.85, 4.14) * mm, "end": v(-3.71, 4.06) * mm});
            skArc(sketch, "E295", {"start": v(-3.97, 4.25) * mm, "mid": v(-4.06, 4.3) * mm, "end": v(-4.16, 4.27) * mm});
            skArc(sketch, "E296", {"start": v(-3.12, 4.1) * mm, "mid": v(-2.94, 4.34) * mm, "end": v(-2.9, 4.64) * mm});
            skArc(sketch, "E297", {"start": v(-2.9, 4.64) * mm, "mid": v(-2.94, 4.8) * mm, "end": v(-3, 4.95) * mm});
            skArc(sketch, "E298", {"start": v(-2.97, 5.14) * mm, "mid": v(-3.02, 5.05) * mm, "end": v(-3, 4.95) * mm});
            skArc(sketch, "E299", {"start": v(-4.85, 2.7) * mm, "mid": v(-4.54, 2.73) * mm, "end": v(-4.3, 2.92) * mm});
            skArc(sketch, "E300", {"start": v(-5.15, 2.8) * mm, "mid": v(-5, 2.74) * mm, "end": v(-4.85, 2.7) * mm});
            skArc(sketch, "E301", {"start": v(-5.15, 2.8) * mm, "mid": v(-5.25, 2.82) * mm, "end": v(-5.34, 2.76) * mm});
            skArc(sketch, "E302", {"start": v(-4.3, 2.92) * mm, "mid": v(-4.2, 3.2) * mm, "end": v(-4.26, 3.5) * mm});
            skArc(sketch, "E303", {"start": v(-4.26, 3.5) * mm, "mid": v(-4.35, 3.64) * mm, "end": v(-4.45, 3.76) * mm});
            skArc(sketch, "E304", {"start": v(-4.47, 3.96) * mm, "mid": v(-4.5, 3.86) * mm, "end": v(-4.45, 3.76) * mm});
            skArc(sketch, "E305", {"start": v(-5.5, 1.06) * mm, "mid": v(-5.23, 1.19) * mm, "end": v(-5.05, 1.44) * mm});
            skArc(sketch, "E306", {"start": v(-5.83, 1.07) * mm, "mid": v(-5.67, 1.05) * mm, "end": v(-5.5, 1.06) * mm});
            skArc(sketch, "E307", {"start": v(-5.83, 1.07) * mm, "mid": v(-5.93, 1.05) * mm, "end": v(-6, 0.97) * mm});
            skArc(sketch, "E308", {"start": v(-5.05, 1.44) * mm, "mid": v(-5.04, 1.75) * mm, "end": v(-5.2, 2.01) * mm});
            skArc(sketch, "E309", {"start": v(-5.2, 2.01) * mm, "mid": v(-5.32, 2.11) * mm, "end": v(-5.46, 2.2) * mm});
            skArc(sketch, "E310", {"start": v(-5.54, 2.38) * mm, "mid": v(-5.53, 2.27) * mm, "end": v(-5.46, 2.2) * mm});
            skArc(sketch, "E311", {"start": v(-5.63, -0.7) * mm, "mid": v(-5.4, -0.5) * mm, "end": v(-5.31, -0.2) * mm});
            skArc(sketch, "E312", {"start": v(-5.93, -0.8) * mm, "mid": v(-5.78, -0.76) * mm, "end": v(-5.63, -0.7) * mm});
            skArc(sketch, "E313", {"start": v(-5.93, -0.8) * mm, "mid": v(-6.03, -0.84) * mm, "end": v(-6.06, -0.94) * mm});
            skArc(sketch, "E314", {"start": v(-5.31, -0.2) * mm, "mid": v(-5.4, 0.1) * mm, "end": v(-5.63, 0.3) * mm});
            skArc(sketch, "E315", {"start": v(-5.63, 0.3) * mm, "mid": v(-5.78, 0.35) * mm, "end": v(-5.93, 0.39) * mm});
            skArc(sketch, "E316", {"start": v(-6.06, 0.54) * mm, "mid": v(-6.03, 0.44) * mm, "end": v(-5.93, 0.39) * mm});
            skArc(sketch, "E317", {"start": v(-5.2, -2.42) * mm, "mid": v(-5.04, -2.15) * mm, "end": v(-5.05, -1.85) * mm});
            skArc(sketch, "E318", {"start": v(-5.46, -2.6) * mm, "mid": v(-5.32, -2.52) * mm, "end": v(-5.2, -2.42) * mm});
            skArc(sketch, "E319", {"start": v(-5.46, -2.6) * mm, "mid": v(-5.53, -2.68) * mm, "end": v(-5.54, -2.78) * mm});
            skArc(sketch, "E320", {"start": v(-5.05, -1.85) * mm, "mid": v(-5.23, -1.6) * mm, "end": v(-5.5, -1.47) * mm});
            skArc(sketch, "E321", {"start": v(-5.5, -1.47) * mm, "mid": v(-5.67, -1.46) * mm, "end": v(-5.83, -1.47) * mm});
            skArc(sketch, "E322", {"start": v(-6, -1.37) * mm, "mid": v(-5.93, -1.46) * mm, "end": v(-5.83, -1.47) * mm});
            skArc(sketch, "E323", {"start": v(-4.26, -3.91) * mm, "mid": v(-4.2, -3.61) * mm, "end": v(-4.3, -3.33) * mm});
            skArc(sketch, "E324", {"start": v(-4.45, -4.17) * mm, "mid": v(-4.35, -4.05) * mm, "end": v(-4.26, -3.91) * mm});
            skArc(sketch, "E325", {"start": v(-4.45, -4.17) * mm, "mid": v(-4.5, -4.26) * mm, "end": v(-4.47, -4.37) * mm});
            skArc(sketch, "E326", {"start": v(-4.3, -3.33) * mm, "mid": v(-4.54, -3.14) * mm, "end": v(-4.85, -3.1) * mm});
            skArc(sketch, "E327", {"start": v(-4.85, -3.1) * mm, "mid": v(-5, -3.15) * mm, "end": v(-5.15, -3.21) * mm});
            skArc(sketch, "E328", {"start": v(-5.34, -3.17) * mm, "mid": v(-5.25, -3.23) * mm, "end": v(-5.15, -3.21) * mm});
            skArc(sketch, "E329", {"start": v(-2.9, -5.05) * mm, "mid": v(-2.94, -4.74) * mm, "end": v(-3.12, -4.5) * mm});
            skArc(sketch, "E330", {"start": v(-3, -5.35) * mm, "mid": v(-2.94, -5.2) * mm, "end": v(-2.9, -5.05) * mm});
            skArc(sketch, "E331", {"start": v(-3, -5.35) * mm, "mid": v(-3.02, -5.46) * mm, "end": v(-2.97, -5.54) * mm});
            skArc(sketch, "E332", {"start": v(-3.12, -4.5) * mm, "mid": v(-3.41, -4.4) * mm, "end": v(-3.71, -4.46) * mm});
            skArc(sketch, "E333", {"start": v(-3.71, -4.46) * mm, "mid": v(-3.85, -4.55) * mm, "end": v(-3.97, -4.66) * mm});
            skArc(sketch, "E334", {"start": v(-4.16, -4.67) * mm, "mid": v(-4.06, -4.7) * mm, "end": v(-3.97, -4.66) * mm});
            skArc(sketch, "E335", {"start": v(-1.26, -5.7) * mm, "mid": v(-1.39, -5.43) * mm, "end": v(-1.64, -5.26) * mm});
            skArc(sketch, "E336", {"start": v(-1.27, -6.03) * mm, "mid": v(-1.25, -5.87) * mm, "end": v(-1.26, -5.7) * mm});
            skArc(sketch, "E337", {"start": v(-1.27, -6.03) * mm, "mid": v(-1.25, -6.13) * mm, "end": v(-1.17, -6.2) * mm});
            skArc(sketch, "E338", {"start": v(-1.64, -5.26) * mm, "mid": v(-1.95, -5.25) * mm, "end": v(-2.21, -5.4) * mm});
            skArc(sketch, "E339", {"start": v(-2.21, -5.4) * mm, "mid": v(-2.32, -5.52) * mm, "end": v(-2.4, -5.66) * mm});
            skArc(sketch, "E340", {"start": v(-2.58, -5.74) * mm, "mid": v(-2.47, -5.74) * mm, "end": v(-2.4, -5.66) * mm});
            skArc(sketch, "E341", {"start": v(0.5, -5.83) * mm, "mid": v(0.3, -5.6) * mm, "end": v(0, -5.52) * mm});
            skArc(sketch, "E342", {"start": v(0.6, -6.14) * mm, "mid": v(0.56, -5.98) * mm, "end": v(0.5, -5.83) * mm});
            skArc(sketch, "E343", {"start": v(0.6, -6.14) * mm, "mid": v(0.64, -6.23) * mm, "end": v(0.74, -6.27) * mm});
            skArc(sketch, "E344", {"start": v(0, -5.52) * mm, "mid": v(-0.3, -5.6) * mm, "end": v(-0.5, -5.83) * mm});
            skArc(sketch, "E345", {"start": v(-0.5, -5.83) * mm, "mid": v(-0.56, -5.98) * mm, "end": v(-0.6, -6.14) * mm});
            skArc(sketch, "E346", {"start": v(-0.74, -6.27) * mm, "mid": v(-0.64, -6.23) * mm, "end": v(-0.6, -6.14) * mm});
            skArc(sketch, "E347", {"start": v(2.21, -5.4) * mm, "mid": v(1.95, -5.25) * mm, "end": v(1.64, -5.26) * mm});
            skArc(sketch, "E348", {"start": v(2.4, -5.66) * mm, "mid": v(2.32, -5.52) * mm, "end": v(2.21, -5.4) * mm});
            skArc(sketch, "E349", {"start": v(2.4, -5.66) * mm, "mid": v(2.47, -5.74) * mm, "end": v(2.58, -5.74) * mm});
            skArc(sketch, "E350", {"start": v(1.64, -5.26) * mm, "mid": v(1.39, -5.43) * mm, "end": v(1.26, -5.7) * mm});
            skArc(sketch, "E351", {"start": v(1.26, -5.7) * mm, "mid": v(1.25, -5.87) * mm, "end": v(1.27, -6.03) * mm});
            skArc(sketch, "E352", {"start": v(1.17, -6.2) * mm, "mid": v(1.25, -6.13) * mm, "end": v(1.27, -6.03) * mm});
            skArc(sketch, "E353", {"start": v(3.71, -4.46) * mm, "mid": v(3.41, -4.4) * mm, "end": v(3.12, -4.5) * mm});
            skArc(sketch, "E354", {"start": v(3.97, -4.66) * mm, "mid": v(3.85, -4.55) * mm, "end": v(3.71, -4.46) * mm});
            skArc(sketch, "E355", {"start": v(3.97, -4.66) * mm, "mid": v(4.06, -4.7) * mm, "end": v(4.16, -4.67) * mm});
            skArc(sketch, "E356", {"start": v(3.12, -4.5) * mm, "mid": v(2.94, -4.74) * mm, "end": v(2.9, -5.05) * mm});
            skArc(sketch, "E357", {"start": v(2.9, -5.05) * mm, "mid": v(2.94, -5.2) * mm, "end": v(3, -5.35) * mm});
            skArc(sketch, "E358", {"start": v(2.97, -5.54) * mm, "mid": v(3.02, -5.46) * mm, "end": v(3, -5.35) * mm});
            skArc(sketch, "E359", {"start": v(4.85, -3.1) * mm, "mid": v(4.54, -3.14) * mm, "end": v(4.3, -3.33) * mm});
            skArc(sketch, "E360", {"start": v(5.15, -3.21) * mm, "mid": v(5, -3.15) * mm, "end": v(4.85, -3.1) * mm});
            skArc(sketch, "E361", {"start": v(5.15, -3.21) * mm, "mid": v(5.25, -3.23) * mm, "end": v(5.34, -3.17) * mm});
            skArc(sketch, "E362", {"start": v(4.3, -3.33) * mm, "mid": v(4.2, -3.61) * mm, "end": v(4.26, -3.91) * mm});
            skArc(sketch, "E363", {"start": v(4.26, -3.91) * mm, "mid": v(4.35, -4.05) * mm, "end": v(4.45, -4.17) * mm});
            skArc(sketch, "E364", {"start": v(4.47, -4.37) * mm, "mid": v(4.5, -4.26) * mm, "end": v(4.45, -4.17) * mm});
            skArc(sketch, "E365", {"start": v(5.5, -1.47) * mm, "mid": v(5.23, -1.6) * mm, "end": v(5.05, -1.85) * mm});
            skArc(sketch, "E366", {"start": v(5.83, -1.47) * mm, "mid": v(5.67, -1.46) * mm, "end": v(5.5, -1.47) * mm});
            skArc(sketch, "E367", {"start": v(5.83, -1.47) * mm, "mid": v(5.93, -1.46) * mm, "end": v(6, -1.37) * mm});
            skArc(sketch, "E368", {"start": v(5.05, -1.85) * mm, "mid": v(5.04, -2.15) * mm, "end": v(5.2, -2.42) * mm});
            skArc(sketch, "E369", {"start": v(5.2, -2.42) * mm, "mid": v(5.32, -2.52) * mm, "end": v(5.46, -2.6) * mm});
            skArc(sketch, "E370", {"start": v(5.54, -2.78) * mm, "mid": v(5.53, -2.68) * mm, "end": v(5.46, -2.6) * mm});
            skArc(sketch, "E371", {"start": v(5.63, 0.3) * mm, "mid": v(5.4, 0.1) * mm, "end": v(5.31, -0.2) * mm});
            skArc(sketch, "E372", {"start": v(5.93, 0.39) * mm, "mid": v(5.78, 0.35) * mm, "end": v(5.63, 0.3) * mm});
            skArc(sketch, "E373", {"start": v(5.93, 0.39) * mm, "mid": v(6.03, 0.44) * mm, "end": v(6.06, 0.54) * mm});
            skArc(sketch, "E374", {"start": v(5.31, -0.2) * mm, "mid": v(5.4, -0.5) * mm, "end": v(5.63, -0.7) * mm});
            skArc(sketch, "E375", {"start": v(5.63, -0.7) * mm, "mid": v(5.78, -0.76) * mm, "end": v(5.93, -0.8) * mm});
            skArc(sketch, "E376", {"start": v(6.06, -0.94) * mm, "mid": v(6.03, -0.84) * mm, "end": v(5.93, -0.8) * mm});
            skArc(sketch, "E377", {"start": v(5.2, 2.01) * mm, "mid": v(5.04, 1.75) * mm, "end": v(5.05, 1.44) * mm});
            skArc(sketch, "E378", {"start": v(5.46, 2.2) * mm, "mid": v(5.32, 2.11) * mm, "end": v(5.2, 2.01) * mm});
            skArc(sketch, "E379", {"start": v(5.46, 2.2) * mm, "mid": v(5.53, 2.27) * mm, "end": v(5.54, 2.38) * mm});
            skArc(sketch, "E380", {"start": v(5.05, 1.44) * mm, "mid": v(5.23, 1.19) * mm, "end": v(5.5, 1.06) * mm});
            skArc(sketch, "E381", {"start": v(5.5, 1.06) * mm, "mid": v(5.67, 1.05) * mm, "end": v(5.83, 1.07) * mm});
            skArc(sketch, "E382", {"start": v(6, 0.97) * mm, "mid": v(5.93, 1.05) * mm, "end": v(5.83, 1.07) * mm});
            skArc(sketch, "E383", {"start": v(4.26, 3.5) * mm, "mid": v(4.2, 3.2) * mm, "end": v(4.3, 2.92) * mm});
            skArc(sketch, "E384", {"start": v(4.45, 3.76) * mm, "mid": v(4.35, 3.64) * mm, "end": v(4.26, 3.5) * mm});
            skArc(sketch, "E385", {"start": v(4.45, 3.76) * mm, "mid": v(4.5, 3.86) * mm, "end": v(4.47, 3.96) * mm});
            skArc(sketch, "E386", {"start": v(4.3, 2.92) * mm, "mid": v(4.54, 2.73) * mm, "end": v(4.85, 2.7) * mm});
            skArc(sketch, "E387", {"start": v(4.85, 2.7) * mm, "mid": v(5, 2.74) * mm, "end": v(5.15, 2.8) * mm});
            skArc(sketch, "E388", {"start": v(5.34, 2.76) * mm, "mid": v(5.25, 2.82) * mm, "end": v(5.15, 2.8) * mm});
            skArc(sketch, "E389", {"start": v(2.9, 4.64) * mm, "mid": v(2.94, 4.34) * mm, "end": v(3.12, 4.1) * mm});
            skArc(sketch, "E390", {"start": v(3, 4.95) * mm, "mid": v(2.94, 4.8) * mm, "end": v(2.9, 4.64) * mm});
            skArc(sketch, "E391", {"start": v(3, 4.95) * mm, "mid": v(3.02, 5.05) * mm, "end": v(2.97, 5.14) * mm});
            skArc(sketch, "E392", {"start": v(3.12, 4.1) * mm, "mid": v(3.41, 4) * mm, "end": v(3.71, 4.06) * mm});
            skArc(sketch, "E393", {"start": v(3.71, 4.06) * mm, "mid": v(3.85, 4.14) * mm, "end": v(3.97, 4.25) * mm});
            skArc(sketch, "E394", {"start": v(4.16, 4.27) * mm, "mid": v(4.06, 4.3) * mm, "end": v(3.97, 4.25) * mm});
            skArc(sketch, "E395", {"start": v(1.26, 5.3) * mm, "mid": v(1.39, 5.02) * mm, "end": v(1.64, 4.85) * mm});
            skArc(sketch, "E396", {"start": v(1.27, 5.62) * mm, "mid": v(1.25, 5.46) * mm, "end": v(1.26, 5.3) * mm});
            skArc(sketch, "E397", {"start": v(1.27, 5.62) * mm, "mid": v(1.25, 5.73) * mm, "end": v(1.17, 5.8) * mm});
            skArc(sketch, "E398", {"start": v(1.64, 4.85) * mm, "mid": v(1.95, 4.84) * mm, "end": v(2.21, 5) * mm});
            skArc(sketch, "E399", {"start": v(2.21, 5) * mm, "mid": v(2.32, 5.12) * mm, "end": v(2.4, 5.26) * mm});
            skArc(sketch, "E400", {"start": v(2.58, 5.34) * mm, "mid": v(2.47, 5.33) * mm, "end": v(2.4, 5.26) * mm});
            skArc(sketch, "E401", {"start": v(-2.58, 5.34) * mm, "mid": v(-2.77, 5.24) * mm, "end": v(-2.97, 5.14) * mm});
            skArc(sketch, "E402", {"start": v(-4.16, 4.27) * mm, "mid": v(2.24, -5.89) * mm, "end": v(0, 5.9) * mm});
            skArc(sketch, "E403", {"start": v(-0.74, 5.86) * mm, "mid": v(-0.96, 5.83) * mm, "end": v(-1.17, 5.8) * mm});
            skCircle(sketch, "E404", {"center": v(0, -0.2) * mm, "radius": 4 * mm});
            skLineSegment(sketch, "E405", {"start": v(-0.98, 12.23) * mm, "end": v(-0.98, 12.66) * mm});
            skLineSegment(sketch, "E406", {"start": v(0.98, 12.23) * mm, "end": v(0.98, 12.66) * mm});
            skSolve(sketch);
        }
        {
            var Q0;
            Q0 = qSketchRegion(id + "F0", true);
            var Q1;
            Q1=makeQuery(id+"F0.imprint","IMPRINT",FACE,{"disambiguationData":[TD([[makeQuery(id+"F0.imprint","IMPRINT",EDGE,{"derivedFrom":sQuery(id+"F0.wireOp",EDGE,"E281")}),-1.0]])]});
            var Q2;
            Q2=makeQuery(id+"F0.imprint","IMPRINT",FACE,{"disambiguationData":[TD([[makeQuery(id+"F0.imprint","IMPRINT",EDGE,{"derivedFrom":sQuery(id+"F0.wireOp",EDGE,"E299")}),1.0]])]});
            var Q3;
            Q3=makeQuery(id+"F0.imprint","IMPRINT",FACE,{"disambiguationData":[TD([[makeQuery(id+"F0.imprint","IMPRINT",EDGE,{"derivedFrom":sQuery(id+"F0.wireOp",EDGE,"E305")}),1.0]])]});
            var Q4;
            Q4=makeQuery(id+"F0.imprint","IMPRINT",FACE,{"disambiguationData":[TD([[makeQuery(id+"F0.imprint","IMPRINT",EDGE,{"derivedFrom":sQuery(id+"F0.wireOp",EDGE,"E311")}),1.0]])]});
            var Q5;
            Q5=makeQuery(id+"F0.imprint","IMPRINT",FACE,{"disambiguationData":[TD([[makeQuery(id+"F0.imprint","IMPRINT",EDGE,{"derivedFrom":sQuery(id+"F0.wireOp",EDGE,"E317")}),1.0]])]});
            var Q6;
            Q6=makeQuery(id+"F0.imprint","IMPRINT",FACE,{"disambiguationData":[TD([[makeQuery(id+"F0.imprint","IMPRINT",EDGE,{"derivedFrom":sQuery(id+"F0.wireOp",EDGE,"E323")}),1.0]])]});
            var Q7;
            Q7=makeQuery(id+"F0.imprint","IMPRINT",FACE,{"disambiguationData":[TD([[makeQuery(id+"F0.imprint","IMPRINT",EDGE,{"derivedFrom":sQuery(id+"F0.wireOp",EDGE,"E329")}),1.0]])]});
            var Q8;
            Q8=makeQuery(id+"F0.imprint","IMPRINT",FACE,{"disambiguationData":[TD([[makeQuery(id+"F0.imprint","IMPRINT",EDGE,{"derivedFrom":sQuery(id+"F0.wireOp",EDGE,"E335")}),1.0]])]});
            var Q9;
            Q9=makeQuery(id+"F0.imprint","IMPRINT",FACE,{"disambiguationData":[TD([[makeQuery(id+"F0.imprint","IMPRINT",EDGE,{"derivedFrom":sQuery(id+"F0.wireOp",EDGE,"E341")}),1.0]])]});
            var Q10;
            Q10=makeQuery(id+"F0.imprint","IMPRINT",FACE,{"disambiguationData":[TD([[makeQuery(id+"F0.imprint","IMPRINT",EDGE,{"derivedFrom":sQuery(id+"F0.wireOp",EDGE,"E347")}),1.0]])]});
            var Q11;
            Q11=makeQuery(id+"F0.imprint","IMPRINT",FACE,{"disambiguationData":[TD([[makeQuery(id+"F0.imprint","IMPRINT",EDGE,{"derivedFrom":sQuery(id+"F0.wireOp",EDGE,"E353")}),1.0]])]});
            var Q12;
            Q12=makeQuery(id+"F0.imprint","IMPRINT",FACE,{"disambiguationData":[TD([[makeQuery(id+"F0.imprint","IMPRINT",EDGE,{"derivedFrom":sQuery(id+"F0.wireOp",EDGE,"E359")}),1.0]])]});
            var Q13;
            Q13=makeQuery(id+"F0.imprint","IMPRINT",FACE,{"disambiguationData":[TD([[makeQuery(id+"F0.imprint","IMPRINT",EDGE,{"derivedFrom":sQuery(id+"F0.wireOp",EDGE,"E365")}),1.0]])]});
            var Q14;
            Q14=makeQuery(id+"F0.imprint","IMPRINT",FACE,{"disambiguationData":[TD([[makeQuery(id+"F0.imprint","IMPRINT",EDGE,{"derivedFrom":sQuery(id+"F0.wireOp",EDGE,"E371")}),1.0]])]});
            var Q15;
            Q15=makeQuery(id+"F0.imprint","IMPRINT",FACE,{"disambiguationData":[TD([[makeQuery(id+"F0.imprint","IMPRINT",EDGE,{"derivedFrom":sQuery(id+"F0.wireOp",EDGE,"E377")}),1.0]])]});
            var Q16;
            Q16=makeQuery(id+"F0.imprint","IMPRINT",FACE,{"disambiguationData":[TD([[makeQuery(id+"F0.imprint","IMPRINT",EDGE,{"derivedFrom":sQuery(id+"F0.wireOp",EDGE,"E383")}),1.0]])]});
            var Q17;
            Q17=makeQuery(id+"F0.imprint","IMPRINT",FACE,{"disambiguationData":[TD([[makeQuery(id+"F0.imprint","IMPRINT",EDGE,{"derivedFrom":sQuery(id+"F0.wireOp",EDGE,"E389")}),1.0]])]});
            var Q18;
            Q18=makeQuery(id+"F0.imprint","IMPRINT",FACE,{"disambiguationData":[TD([[makeQuery(id+"F0.imprint","IMPRINT",EDGE,{"derivedFrom":sQuery(id+"F0.wireOp",EDGE,"E395")}),1.0]])]});
            extrude(context, id + "F1", {"entities" : qUnion([Q0, Q1, Q2, Q3, Q4, Q5, Q6, Q7, Q8, Q9, Q10, Q11, Q12, Q13, Q14, Q15, Q16, Q17, Q18]), "depth" : 7 * mm});
        }
        {
            var Q0;
            Q0=makeQuery(id+"F0.imprint","IMPRINT",FACE,{"disambiguationData":[TD([[makeQuery(id+"F0.imprint","IMPRINT",EDGE,{"derivedFrom":sQuery(id+"F0.wireOp",EDGE,"E281")}),-1.0]])]});
            extrude(context, id + "F2", {"entities" : qUnion([Q0]), "depth" : 14 * mm});
        }
    });
